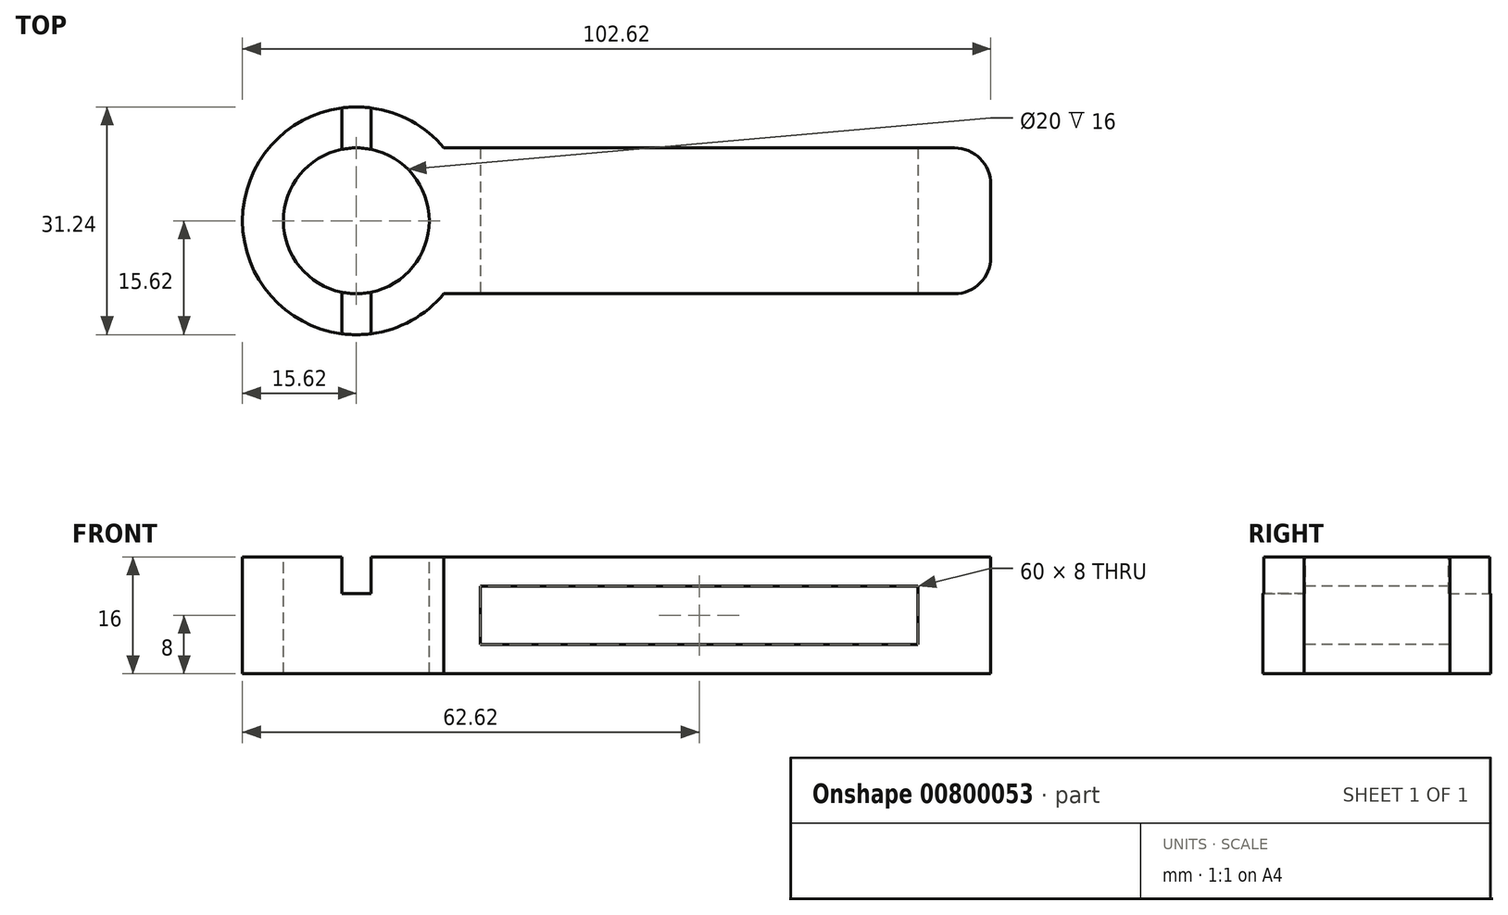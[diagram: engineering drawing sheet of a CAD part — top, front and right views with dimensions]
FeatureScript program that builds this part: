
annotation { "Feature Type Name" : "Feature", "Feature Type Description" : "" }
export const myFeature = defineFeature(function(context is Context, id is Id, definition is map)
    precondition{}
    {
        {
            var Q0;
            Q0=qCreatedBy(makeId("Top.planeOp"),FACE);
            var sketch = newSketch(context, id + "F0", { "sketchPlane" : qUnion([Q0])});
            skLineSegment(sketch, "E0", {"start": v(75, 0) * mm, "end": v(75, 5) * mm});
            skLineSegment(sketch, "E1", {"start": v(70, 10) * mm, "end": v(0, 10) * mm});
            skLineSegment(sketch, "E2", {"start": v(75, 0) * mm, "end": v(75, -5) * mm});
            skLineSegment(sketch, "E3", {"start": v(70, -10) * mm, "end": v(0, -10) * mm});
            skArc(sketch, "E4", {"start": v(0, 10) * mm, "mid": v(-27.62, 0) * mm, "end": v(0, -10) * mm});
            skPoint(sketch, "E5.visualSharp", {"position": v(75, 10) * mm});
            skArc(sketch, "E5.filletArc", {"start": v(75, 5) * mm, "mid": v(73.54, 8.54) * mm, "end": v(70, 10) * mm});
            skPoint(sketch, "E6.visualSharp", {"position": v(75, -10) * mm});
            skArc(sketch, "E6.filletArc", {"start": v(70, -10) * mm, "mid": v(73.54, -8.54) * mm, "end": v(75, -5) * mm});
            skSolve(sketch);
        }
        {
            var Q0;
            Q0=makeQuery(id+"F0.imprint","IMPRINT",FACE,{"disambiguationData":[TD([[makeQuery(id+"F0.imprint","IMPRINT",EDGE,{"derivedFrom":sQuery(id+"F0.wireOp",EDGE,"E0")}),1.0]])]});
            extrude(context, id + "F1", {"entities" : qUnion([Q0]), "depth" : 16 * mm, "offsetDistance" : 25 * mm});
        }
        {
            var Q0;
            Q0=makeQuery(id+"F1.opExtrude","CAP_FACE",FACE,{"disambiguationData":[OSD([sQuery(id+"F0.wireOp",EDGE,"E0"),sQuery(id+"F0.wireOp",EDGE,"E1"),sQuery(id+"F0.wireOp",EDGE,"E2"),sQuery(id+"F0.wireOp",EDGE,"E3"),sQuery(id+"F0.wireOp",EDGE,"E4"),sQuery(id+"F0.wireOp",EDGE,"E5.filletArc"),sQuery(id+"F0.wireOp",EDGE,"E6.filletArc")])],"isStart":false});
            var sketch = newSketch(context, id + "F2", { "sketchPlane" : qUnion([Q0])});
            skCircle(sketch, "E7", {"center": v(-12, 0) * mm, "radius": 10 * mm});
            skSolve(sketch);
        }
        {
            var Q0;
            Q0=makeQuery(id+"F2.imprint","IMPRINT",FACE,{"disambiguationData":[TD([[makeQuery(id+"F2.imprint","IMPRINT",EDGE,{"derivedFrom":sQuery(id+"F2.wireOp",EDGE,"E7")}),1.0]])]});
            extrude(context, id + "F3", {"entities" : qUnion([Q0]), "operationType" : NewBodyOperationType.REMOVE, "oppositeDirection" : true, "depth" : 25 * mm, "offsetDistance" : 25 * mm});
        }
        {
            var Q0;
            Q0=makeQuery(id+"F1.opExtrude","SWEPT_FACE",FACE,{"disambiguationData":[OSD([sQuery(id+"F0.wireOp",EDGE,"E3")])]});
            var sketch = newSketch(context, id + "F4", { "sketchPlane" : qUnion([Q0])});
            skLineSegment(sketch, "E8", {"start": v(0, 0) * mm, "end": v(5, 0) * mm, "construction": true});
            skLineSegment(sketch, "E9", {"start": v(5, 0) * mm, "end": v(5, 4) * mm, "construction": true});
            skLineSegment(sketch, "E10", {"start": v(70, 16) * mm, "end": v(70, 12) * mm, "construction": true});
            skLineSegment(sketch, "E11", {"start": v(70, 12) * mm, "end": v(65, 12) * mm, "construction": true});
            skLineSegment(sketch, "E12.bottom", {"start": v(5, 4) * mm, "end": v(65, 4) * mm});
            skLineSegment(sketch, "E12.top", {"start": v(5, 12) * mm, "end": v(65, 12) * mm});
            skLineSegment(sketch, "E12.left", {"start": v(5, 4) * mm, "end": v(5, 12) * mm});
            skLineSegment(sketch, "E12.right", {"start": v(65, 4) * mm, "end": v(65, 12) * mm});
            skSolve(sketch);
        }
        {
            var Q0;
            Q0=makeQuery(id+"F4.imprint","IMPRINT",FACE,{"disambiguationData":[TD([[makeQuery(id+"F4.imprint","IMPRINT",EDGE,{"derivedFrom":sQuery(id+"F4.wireOp",EDGE,"E12.bottom")}),1.0]])]});
            extrude(context, id + "F5", {"entities" : qUnion([Q0]), "operationType" : NewBodyOperationType.REMOVE, "oppositeDirection" : true, "depth" : 25 * mm, "offsetDistance" : 25 * mm});
        }
        {
            var Q0;
            Q0=makeQuery(id+"F1.opExtrude","CAP_FACE",FACE,{"disambiguationData":[OSD([sQuery(id+"F0.wireOp",EDGE,"E0"),sQuery(id+"F0.wireOp",EDGE,"E1"),sQuery(id+"F0.wireOp",EDGE,"E2"),sQuery(id+"F0.wireOp",EDGE,"E3"),sQuery(id+"F0.wireOp",EDGE,"E4"),sQuery(id+"F0.wireOp",EDGE,"E5.filletArc"),sQuery(id+"F0.wireOp",EDGE,"E6.filletArc")])],"isStart":false});
            var sketch = newSketch(context, id + "F6", { "sketchPlane" : qUnion([Q0])});
            skArc(sketch, "E13", {"start": v(-14, -15.5) * mm, "mid": v(-12, -15.62) * mm, "end": v(-10, -15.5) * mm});
            skLineSegment(sketch, "E14", {"start": v(-14, -15.5) * mm, "end": v(-14, -9.8) * mm});
            skPoint(sketch, "E15.end.orphan", {"position": v(-10, -12.81) * mm});
            skLineSegment(sketch, "E16", {"start": v(-10, -9.8) * mm, "end": v(-10, -15.5) * mm});
            skLineSegment(sketch, "E17", {"start": v(-14, -9.8) * mm, "end": v(-14, 15.5) * mm});
            skLineSegment(sketch, "E18", {"start": v(-10, -9.8) * mm, "end": v(-10, 15.5) * mm});
            skSolve(sketch);
        }
        {
            var Q0;
            {var subQ0=sQuery(id+"F6.wireOp",EDGE,"E17");var subQ1=makeQuery(id+"F1.opExtrude","CAP_EDGE",EDGE,{"disambiguationData":[OSD([sQuery(id+"F0.wireOp",EDGE,"E4")])],"isStart":false});var subQ2=makeQuery(id+"F6.imprint","INTERSECT",VERTEX,{"derivedFrom":[subQ1,subQ0]});Q0=makeQuery(id+"F6.imprint","IMPRINT",FACE,{"disambiguationData":[TD([[makeQuery(id+"F6.imprint","IMPRINT",EDGE,{"disambiguationData":[TD([[subQ2,1.0]])],"derivedFrom":subQ0}),-1.0]])]});}
            var Q1;
            Q1=makeQuery(id+"F6.imprint","IMPRINT",FACE,{"disambiguationData":[TD([[makeQuery(id+"F6.imprint","IMPRINT",EDGE,{"derivedFrom":sQuery(id+"F6.wireOp",EDGE,"E13")}),1.0]])]});
            extrude(context, id + "F7", {"entities" : qUnion([Q0, Q1]), "operationType" : NewBodyOperationType.REMOVE, "oppositeDirection" : true, "depth" : 5 * mm, "offsetDistance" : 25 * mm});
        }
    });
